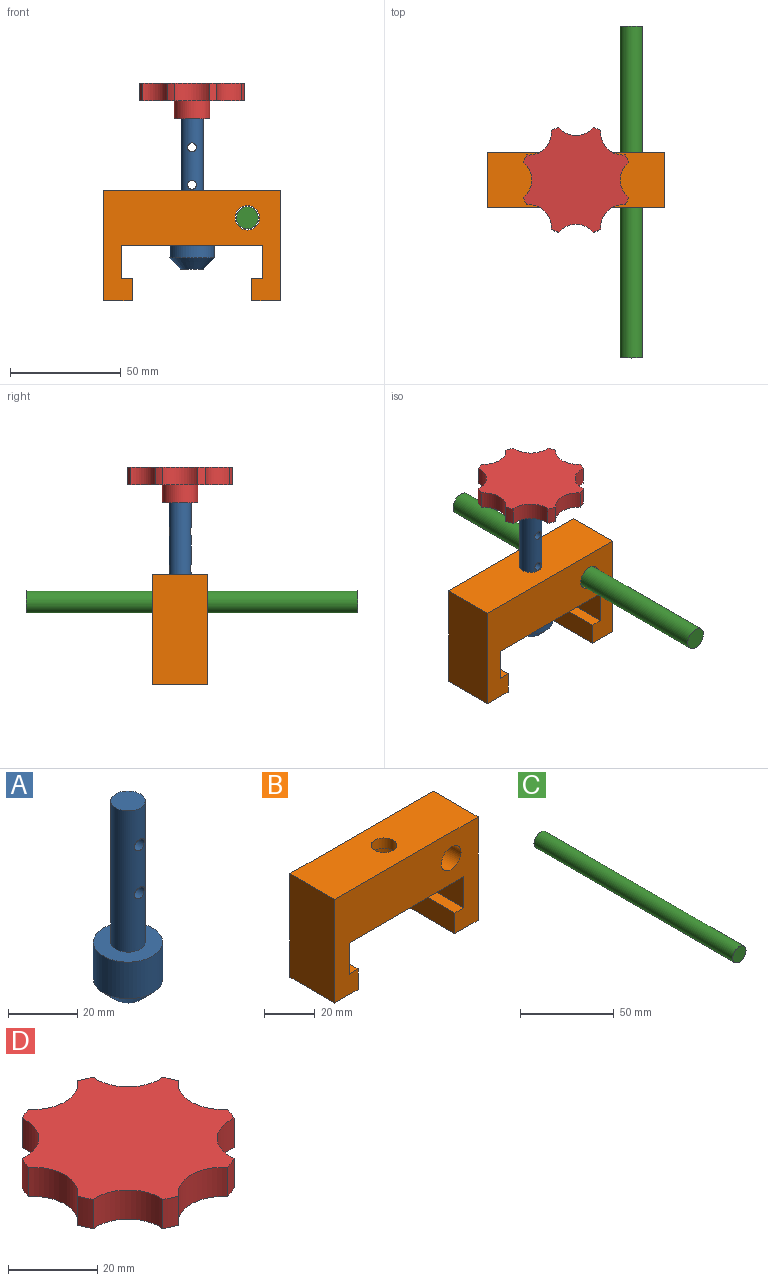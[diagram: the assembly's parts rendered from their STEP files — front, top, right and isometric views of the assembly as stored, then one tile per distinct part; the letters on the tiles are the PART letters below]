
ASSEMBLY  parts=4 mates=3
PART A: 8 faces, bbox 20x20x68 mm
  f0: cylinder r=5mm len=50mm, axis (0,0,1), area 1519.4mm2, adj f1,f4,f6,f7
  f1: plane 10x10mm, normal (0,0,1), area 78.5mm2, adj f0
  f2: plane 10x10mm, normal (0,0,-1), area 78.5mm2, adj f5
  f3: cylinder r=10mm len=20mm, axis (0,0,1), area 816.8mm2, adj f4,f5
  f4: plane 20x20mm, normal (0,0,1), area 235.6mm2, adj f0,f3
  f5: cone r=10mm half-angle=45deg, axis (0,0,1), area 333.2mm2, adj f2,f3
  f6: cylinder r=2mm len=10mm, axis (0,1,0), area 120.5mm2, adj f0
  f7: cylinder r=2mm len=10mm, axis (0,1,0), area 120.5mm2, adj f0
PART B: 18 faces, bbox 80x25x50 mm
  f0: plane 64x25mm, normal (0,0,-1), area 1285.8mm2, adj f1,f11,f12,f13,f16
  f1: plane 25x15mm, normal (-1,0,0), area 375mm2, adj f0,f2,f12,f13
  f2: plane 25x5mm, normal (0,0,1), area 125mm2, adj f1,f3,f12,f13
  f3: plane 25x10mm, normal (-1,0,0), area 250mm2, adj f2,f4,f12,f13
  f4: plane 25x13mm, normal (0,0,-1), area 325mm2, adj f3,f5,f12,f13
  f5: plane 50x25mm, normal (1,0,0), area 1250mm2, adj f4,f6,f12,f13
  f6: plane 80x25mm, normal (0,0,1), area 1921.5mm2, adj f5,f7,f12,f13,f14
  f7: plane 50x25mm, normal (-1,0,0), area 1250mm2, adj f6,f8,f12,f13
  f8: plane 25x13mm, normal (0,0,-1), area 325mm2, adj f7,f9,f12,f13
  f9: plane 25x10mm, normal (1,0,0), area 250mm2, adj f8,f10,f12,f13
  f10: plane 25x5mm, normal (0,0,1), area 125mm2, adj f9,f11,f12,f13
  f11: plane 25x15mm, normal (1,0,0), area 375mm2, adj f0,f10,f12,f13
  f12: plane 80x50mm, normal (0,-1,0), area 2405mm2, adj f0,f1,f2,f3,f4,f5,f6,f7
  f13: plane 80x50mm, normal (0,1,0), area 2405mm2, adj f0,f1,f2,f3,f4,f5,f6,f7
  f14: cylinder r=5mm len=10mm, axis (0,0,-1), area 157.1mm2, adj f6,f15
  f15: plane 20x20mm, normal (0,0,-1), area 235.6mm2, adj f14,f16
  f16: cylinder r=10mm len=20mm, axis (0,0,-1), area 1256.6mm2, adj f0,f15
  f17: cylinder r=5.5mm len=25mm, axis (0,-1,0), area 863.9mm2, adj f12,f13
PART C: 3 faces, bbox 10x150x10 mm
  f0: plane 10x10mm, normal (0,1,0), area 78.5mm2, adj f1
  f1: cylinder r=5mm len=150mm, axis (0,-1,0), area 4712.4mm2, adj f0,f2
  f2: plane 10x10mm, normal (0,-1,0), area 78.5mm2, adj f1
PART D: 22 faces, bbox 47.5x47.5x16 mm
  f0: cylinder r=25mm len=8mm, axis (0,0,1), area 30.1mm2, adj f8,f11,f12,f19
  f1: cylinder r=25mm len=8mm, axis (0,0,1), area 30.1mm2, adj f8,f11,f18,f19
  f2: cylinder r=25mm len=8mm, axis (0,0,1), area 30.1mm2, adj f8,f11,f17,f18
  f3: cylinder r=25mm len=8mm, axis (0,0,1), area 30.1mm2, adj f8,f11,f16,f17
  f4: cylinder r=25mm len=8mm, axis (0,0,1), area 30.1mm2, adj f8,f11,f15,f16
  f5: cylinder r=25mm len=8mm, axis (0,0,1), area 30.1mm2, adj f8,f11,f14,f15
  f6: cylinder r=25mm len=8mm, axis (0,0,1), area 30.1mm2, adj f8,f11,f13,f14
  f7: cylinder r=25mm len=8mm, axis (0,0,1), area 30.1mm2, adj f8,f11,f12,f13
  f8: plane 47.5x47.5mm, normal (0,0,1), area 1532.7mm2, adj f0,f1,f2,f3,f4,f5,f6,f7
  f9: plane 16x16mm, normal (0,0,-1), area 106mm2, adj f10,f20
  f10: cylinder r=8mm len=16mm, axis (0,0,1), area 402.1mm2, adj f9,f11
  f11: plane 47.5x47.5mm, normal (0,0,-1), area 1331.6mm2, adj f0,f1,f2,f3,f4,f5,f6,f7
  f12: cylinder r=10mm len=15.61mm, axis (0,0,1), area 143.3mm2, adj f0,f7,f8,f11
  f13: cylinder r=10mm len=11.1mm, axis (0,0,1), area 143.3mm2, adj f6,f7,f8,f11
  f14: cylinder r=10mm len=15.61mm, axis (0,0,1), area 143.3mm2, adj f5,f6,f8,f11
  f15: cylinder r=10mm len=11.1mm, axis (0,0,1), area 143.3mm2, adj f4,f5,f8,f11
  f16: cylinder r=10mm len=15.61mm, axis (0,0,1), area 143.3mm2, adj f3,f4,f8,f11
  f17: cylinder r=10mm len=11.1mm, axis (0,0,1), area 143.3mm2, adj f2,f3,f8,f11
  f18: cylinder r=10mm len=15.61mm, axis (0,0,1), area 143.3mm2, adj f1,f2,f8,f11
  f19: cylinder r=10mm len=11.1mm, axis (0,0,1), area 143.3mm2, adj f0,f1,f8,f11
  f20: cylinder r=5.5mm len=11mm, axis (0,0,-1), area 345.6mm2, adj f9,f21
  f21: cone r=0mm half-angle=59deg, axis (0,0,-1), area 110.9mm2, adj f20
PLACE A t=(-44.68,30,36.12)mm
PLACE B t=(-44.68,30,46.75)mm fixed
PLACE C t=(-19.68,-50.37,59.25)mm
PLACE D t=(-44.68,30,104.12)mm
MATE slider B.f14 <-> A.f0  axis (0,0,-1) through (-44.68,30,71.75)mm
MATE fastened A.f0 <-> D.f0  axis (0,0,1) through (-44.68,30,104.12)mm
MATE slider C.f1 <-> B.f17  axis (0,-1,0) through (-19.68,24.63,59.25)mm
